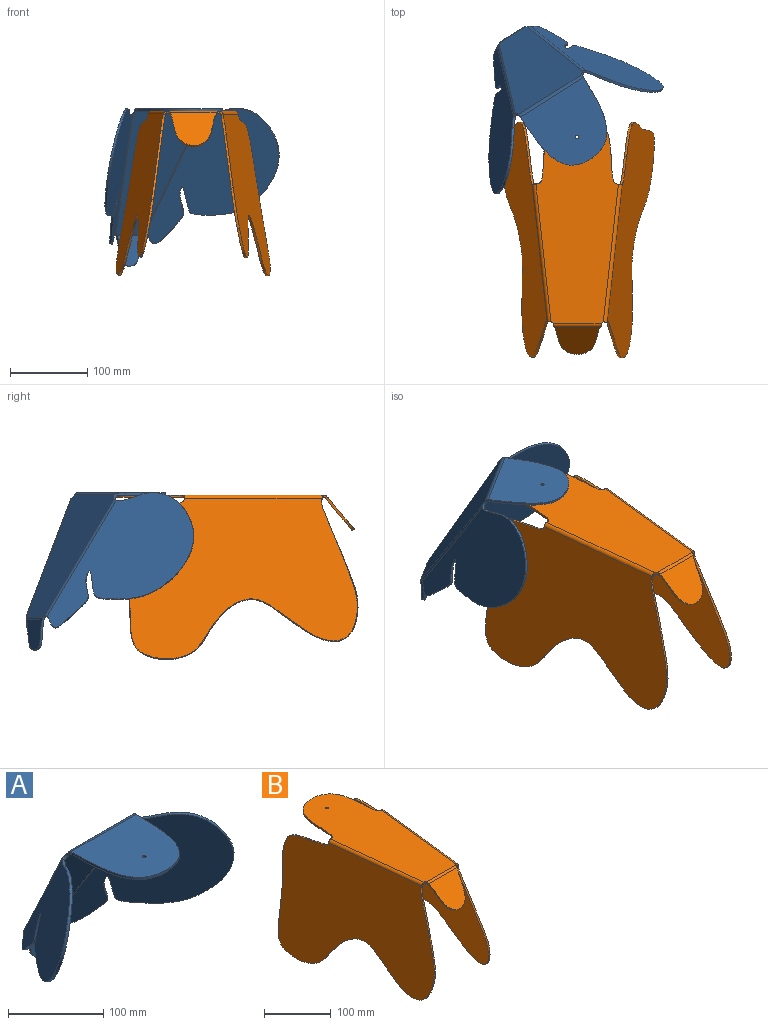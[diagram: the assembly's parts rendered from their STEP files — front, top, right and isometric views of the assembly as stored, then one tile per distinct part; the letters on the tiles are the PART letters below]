
ASSEMBLY  parts=2 mates=1
PART A: 73 faces, bbox 259.7x191.3x206.6 mm
  f0: extruded ~23.99x7.76mm, area 78.3mm2, adj f1,f3,f4,f5
  f1: extruded ~18.34x3.31mm, area 58.3mm2, adj f0,f2,f3,f4
  f2: extruded ~20.11x5.29mm, area 63.3mm2, adj f1,f3,f4,f6
  f3: plane 40.69x38.37mm, normal (0,1,0), area 1160.1mm2, adj f0,f1,f2,f5,f6,f14
  f4: plane 40.69x38.37mm, normal (0,-1,0), area 1160.1mm2, adj f0,f1,f2,f5,f6,f16
  f5: extruded ~14.01x3.09mm, area 43.1mm2, adj f0,f3,f4,f13
  f6: extruded ~16.48x3.39mm, area 50.7mm2, adj f2,f3,f4,f15
  f7: extruded ~6.83x5.68mm, area 21.5mm2, adj f11,f12,f58,f71
  f8: extruded ~4.34x4.24mm, area 12mm2, adj f11,f12,f15,f56
  f9: extruded ~4.06x4.03mm, area 12.1mm2, adj f11,f12,f13,f35
  f10: extruded ~7.14x5.85mm, area 22.4mm2, adj f11,f12,f33,f69
  f11: plane 158.85x103.01mm, normal (0,-0.87,-0.5), area 13392.8mm2, adj f7,f8,f9,f10,f16,f32,f59,f70
  f12: plane 158.85x103.01mm, normal (0,0.87,0.5), area 13392.8mm2, adj f7,f8,f9,f10,f14,f34,f57,f68
  f13: plane 3.27x2.5mm, normal (-1,0,0), area 5.5mm2, adj f5,f9,f14,f16
  f14: cylinder r=5mm len=37.88mm, axis (1,0,0), area 99.2mm2, adj f3,f12,f13,f15
  f15: plane 3.27x2.5mm, normal (1,0,0), area 5.5mm2, adj f6,f8,f14,f16
  f16: cylinder r=2mm len=37.88mm, axis (1,0,0), area 39.7mm2, adj f4,f11,f13,f15
  f17: plane 176.84x161.17mm, normal (-0.75,0.62,0.21), area 17195.4mm2, adj f19,f20,f21,f22,f23,f24,f25,f26
  f18: plane 176.84x161.17mm, normal (0.75,-0.62,-0.21), area 17195.4mm2, adj f19,f20,f21,f22,f23,f24,f25,f26
  f19: extruded ~8.01x6.3mm, area 27.3mm2, adj f17,f18,f35,f36
  f20: extruded ~12.04x8.87mm, area 42.6mm2, adj f17,f18,f21,f36
  f21: plane 20.76x20.45mm, normal (-0.56,-0.44,-0.7), area 87.6mm2, adj f17,f18,f20,f22
  f22: extruded ~24.28x11.41mm, area 83.7mm2, adj f17,f18,f21,f23
  f23: extruded ~24.8x7.62mm, area 77.8mm2, adj f17,f18,f22,f24
  f24: extruded ~18.48x7.77mm, area 56.2mm2, adj f17,f18,f23,f25
  f25: extruded ~17.64x8.77mm, area 56.7mm2, adj f17,f18,f24,f26
  f26: extruded ~14.79x13.54mm, area 52.3mm2, adj f17,f18,f25,f27
  f27: extruded ~87.86x57.74mm, area 373.9mm2, adj f17,f18,f26,f29
  f28: extruded ~14.07x11.88mm, area 48.2mm2, adj f17,f18,f31,f33
  f29: extruded ~49.08x11.13mm, area 153.8mm2, adj f17,f18,f27,f30
  f30: extruded ~28.8x23.75mm, area 119.9mm2, adj f17,f18,f29,f31
  f31: extruded ~44.2x36.25mm, area 168.8mm2, adj f17,f18,f28,f30
  f32: cylinder r=2mm len=150.9mm, axis (0.17,0.49,-0.85), area 307.4mm2, adj f11,f18,f33,f35
  f33: plane 3.77x3.11mm, normal (-0.17,-0.49,0.85), area 9.2mm2, adj f10,f28,f32,f34
  f34: cylinder r=5mm len=151.77mm, axis (0.17,0.49,-0.85), area 768.5mm2, adj f12,f17,f33,f35
  f35: plane 3.77x3.11mm, normal (0.17,0.49,-0.85), area 9.2mm2, adj f9,f19,f32,f34
  f36: extruded ~7.38x7.06mm, area 27.9mm2, adj f17,f18,f19,f20
  f37: extruded ~27.85x21.18mm, area 109.5mm2, adj f38,f51,f53,f54
  f38: extruded ~36.92x10.35mm, area 113.9mm2, adj f37,f39,f53,f54
  f39: extruded ~36.3x22.64mm, area 127.2mm2, adj f38,f40,f53,f54
  f40: extruded ~26.44x22.43mm, area 108mm2, adj f39,f41,f53,f54
  f41: extruded ~44.39x34.78mm, area 164.9mm2, adj f40,f42,f53,f54
  f42: extruded ~17.47x15.89mm, area 63.2mm2, adj f41,f43,f53,f54
  f43: extruded ~8.76x5.78mm, area 27.5mm2, adj f42,f44,f53,f54
  f44: extruded ~19.02x7.48mm, area 57.4mm2, adj f43,f45,f53,f54
  f45: extruded ~8.64x5.55mm, area 27.5mm2, adj f44,f46,f53,f54
  f46: extruded ~24.82x6.78mm, area 76.8mm2, adj f45,f47,f53,f54
  f47: extruded ~12.43x5.06mm, area 36.7mm2, adj f46,f48,f53,f54
  f48: extruded ~12.8x10.64mm, area 46.9mm2, adj f47,f49,f53,f54
  f49: extruded ~20.73x20.47mm, area 87.6mm2, adj f48,f50,f53,f54
  f50: extruded ~12.38x9.32mm, area 43.5mm2, adj f49,f53,f54,f55
  f51: extruded ~45.41x38.2mm, area 176.9mm2, adj f37,f52,f53,f54
  f52: extruded ~15.7x12.92mm, area 54.8mm2, adj f51,f53,f54,f58
  f53: plane 177.09x160.16mm, normal (-0.75,-0.62,-0.21), area 17203.3mm2, adj f37,f38,f39,f40,f41,f42,f43,f44
  f54: plane 177.09x160.16mm, normal (0.75,0.62,0.21), area 17203.3mm2, adj f37,f38,f39,f40,f41,f42,f43,f44
  f55: extruded ~14.65x10.86mm, area 54.4mm2, adj f50,f53,f54,f56
  f56: plane 3.77x3.11mm, normal (-0.17,0.49,-0.85), area 9.2mm2, adj f8,f55,f57,f59
  f57: cylinder r=5mm len=151.78mm, axis (0.17,-0.49,0.85), area 768.8mm2, adj f12,f54,f56,f58
  f58: plane 3.77x3.11mm, normal (0.17,-0.49,0.85), area 9.2mm2, adj f7,f52,f57,f59
  f59: cylinder r=2mm len=150.9mm, axis (0.17,-0.49,0.85), area 307.5mm2, adj f11,f53,f56,f58
  f60: extruded ~10.75x3mm, area 32.3mm2, adj f61,f64,f65,f67
  f61: extruded ~80.79x36.34mm, area 289.2mm2, adj f60,f62,f64,f65
  f62: extruded ~38.1x7.82mm, area 119.2mm2, adj f61,f63,f64,f65
  f63: extruded ~56.09x21.17mm, area 185.4mm2, adj f62,f64,f65,f66
  f64: plane 97.8x95.65mm, normal (0,0,1), area 7819.7mm2, adj f60,f61,f62,f63,f66,f67,f68,f72
  f65: plane 97.8x95.65mm, normal (0,0,-1), area 7819.7mm2, adj f60,f61,f62,f63,f66,f67,f70,f72
  f66: extruded ~30.18x3mm, area 90.7mm2, adj f63,f64,f65,f71
  f67: extruded ~3x1.44mm, area 4.3mm2, adj f60,f64,f65,f69
  f68: cylinder r=5mm len=96.98mm, axis (-1,0,0), area 507.8mm2, adj f12,f64,f69,f71
  f69: plane 4.33x4mm, normal (-1,0,0), area 11mm2, adj f10,f67,f68,f70
  f70: cylinder r=2mm len=96.98mm, axis (-1,0,0), area 203.1mm2, adj f11,f65,f69,f71
  f71: plane 4.33x4mm, normal (1,0,0), area 11mm2, adj f7,f66,f68,f70
  f72: cylinder r=2mm len=4mm, axis (0,0,1), area 37.7mm2, adj f64,f65
PART B: 70 faces, bbox 199.4x320.8x215.7 mm
  f0: extruded ~12.02x10.77mm, area 40.1mm2, adj f1,f4,f5,f7
  f1: extruded ~27.06x23.39mm, area 112.6mm2, adj f0,f2,f4,f5
  f2: extruded ~30.34x13.13mm, area 110.4mm2, adj f1,f3,f4,f5
  f3: extruded ~19.76x17.26mm, area 72.1mm2, adj f2,f4,f5,f6
  f4: plane 62.03x44.64mm, normal (0,0.77,-0.64), area 2504.5mm2, adj f0,f1,f2,f3,f6,f7,f11
  f5: plane 62.03x44.64mm, normal (0,-0.77,0.64), area 2504.5mm2, adj f0,f1,f2,f3,f6,f7,f9
  f6: extruded ~15.56x13.74mm, area 55.7mm2, adj f3,f4,f5,f8
  f7: extruded ~7.36x6.86mm, area 23.3mm2, adj f0,f4,f5,f10
  f8: plane 3.83x3.71mm, normal (-1,0,0), area 9.2mm2, adj f6,f9,f11,f20
  f9: cylinder r=5mm len=61.53mm, axis (1,0,0), area 268.5mm2, adj f5,f8,f10,f22
  f10: plane 3.83x3.71mm, normal (1,0,0), area 9.2mm2, adj f7,f9,f11,f19
  f11: cylinder r=2mm len=61.53mm, axis (1,0,0), area 107.4mm2, adj f4,f8,f10,f21
  f12: extruded ~52.99x11.82mm, area 164.6mm2, adj f13,f14,f16,f17
  f13: extruded ~38.1x30.2mm, area 162.5mm2, adj f12,f16,f17,f18
  f14: extruded ~69.53x28.96mm, area 225.8mm2, adj f12,f15,f16,f17
  f15: extruded ~26.25x7.13mm, area 82.3mm2, adj f14,f16,f17,f34
  f16: plane 306.13x211.08mm, normal (-0.98,0.11,-0.17), area 48358mm2, adj f12,f13,f14,f15,f18,f35,f37,f38
  f17: plane 306.13x211.08mm, normal (0.98,-0.11,0.17), area 48358mm2, adj f12,f13,f14,f15,f18,f33,f37,f38
  f18: extruded ~30.85x10.09mm, area 97.3mm2, adj f13,f16,f17,f37
  f19: extruded ~3x2.89mm, area 11.2mm2, adj f10,f21,f22,f34
  f20: extruded ~3.31x3mm, area 13mm2, adj f8,f21,f22,f53
  f21: plane 275.63x106.54mm, normal (0,0,-1), area 23059.1mm2, adj f11,f19,f20,f27,f28,f29,f30,f31
  f22: plane 275.63x106.54mm, normal (0,0,1), area 23059.1mm2, adj f9,f19,f20,f27,f28,f29,f30,f31
  f23: plane 305.98x209.65mm, normal (-0.98,-0.11,0.17), area 48219.4mm2, adj f25,f26,f50,f54,f55,f56,f57,f58
  f24: plane 305.98x209.65mm, normal (0.98,0.11,-0.17), area 48219.4mm2, adj f25,f26,f52,f54,f55,f56,f57,f58
  f25: extruded ~20.81x6.12mm, area 64.2mm2, adj f23,f24,f53,f68
  f26: extruded ~41.3x12.41mm, area 130.8mm2, adj f23,f24,f65,f69
  f27: extruded ~14.82x8.11mm, area 56.4mm2, adj f21,f22,f28,f36
  f28: extruded ~59.97x9.53mm, area 183.8mm2, adj f21,f22,f27,f29
  f29: extruded ~27.16x19.05mm, area 103.1mm2, adj f21,f22,f28,f30
  f30: extruded ~35.63x10.34mm, area 115mm2, adj f21,f22,f29,f31
  f31: extruded ~65.62x16.93mm, area 209.5mm2, adj f21,f22,f30,f32
  f32: extruded ~18.35x9.17mm, area 69.1mm2, adj f21,f22,f31,f51
  f33: cylinder r=5mm len=178.33mm, axis (-0.11,-0.99,0), area 1248.6mm2, adj f17,f22,f34,f36
  f34: plane 4.9x4.65mm, normal (-0.11,-0.99,0), area 14.7mm2, adj f15,f19,f33,f35
  f35: cylinder r=2mm len=178.01mm, axis (-0.11,-0.99,0), area 499.5mm2, adj f16,f21,f34,f36
  f36: plane 4.9x4.65mm, normal (0.11,0.99,0), area 14.7mm2, adj f27,f33,f35,f49
  f37: extruded ~45.76x32.28mm, area 166.5mm2, adj f16,f17,f18,f38
  f38: extruded ~26.69x13.13mm, area 88.6mm2, adj f16,f17,f37,f39
  f39: extruded ~43.78x20.87mm, area 151.5mm2, adj f16,f17,f38,f40
  f40: extruded ~19.2x14.72mm, area 72.3mm2, adj f16,f17,f39,f41
  f41: extruded ~21.07x13.48mm, area 74.9mm2, adj f16,f17,f40,f42
  f42: extruded ~76.97x18.68mm, area 252.7mm2, adj f16,f17,f41,f43
  f43: extruded ~45.58x13.86mm, area 148.3mm2, adj f16,f17,f42,f44
  f44: extruded ~44.3x10.52mm, area 133.4mm2, adj f16,f17,f43,f45
  f45: extruded ~40.57x9.4mm, area 123mm2, adj f16,f17,f44,f46
  f46: extruded ~43.45x10.52mm, area 132.2mm2, adj f16,f17,f45,f47
  f47: extruded ~41.71x17.33mm, area 143.6mm2, adj f16,f17,f46,f48
  f48: extruded ~21.31x5.57mm, area 63.7mm2, adj f16,f17,f47,f49
  f49: extruded ~15.9x8.95mm, area 58.3mm2, adj f16,f17,f36,f48
  f50: cylinder r=5mm len=178.33mm, axis (-0.11,0.99,0), area 1248.6mm2, adj f22,f23,f51,f53
  f51: plane 4.9x4.65mm, normal (-0.11,0.99,0), area 14.7mm2, adj f32,f50,f52,f54
  f52: cylinder r=2mm len=178.01mm, axis (-0.11,0.99,0), area 499.5mm2, adj f21,f24,f51,f53
  f53: plane 4.9x4.65mm, normal (0.11,-0.99,0), area 14.7mm2, adj f20,f25,f50,f52
  f54: extruded ~15.49x8.3mm, area 55.7mm2, adj f23,f24,f51,f55
  f55: extruded ~20.61x5.51mm, area 61.7mm2, adj f23,f24,f54,f56
  f56: extruded ~37.05x8.76mm, area 115.5mm2, adj f23,f24,f55,f57
  f57: extruded ~45.5x11.63mm, area 143.6mm2, adj f23,f24,f56,f58
  f58: extruded ~40.26x9.3mm, area 122.2mm2, adj f23,f24,f57,f59
  f59: extruded ~43.64x10.36mm, area 131.4mm2, adj f23,f24,f58,f60
  f60: extruded ~83.92x62.27mm, area 394.1mm2, adj f23,f24,f59,f61
  f61: extruded ~17.24x13.48mm, area 65.5mm2, adj f23,f24,f60,f62
  f62: extruded ~34.37x25.98mm, area 130.5mm2, adj f23,f24,f61,f63
  f63: extruded ~41.56x16.31mm, area 138.7mm2, adj f23,f24,f62,f64
  f64: extruded ~34.51x20.25mm, area 119.4mm2, adj f23,f24,f63,f65
  f65: extruded ~31.84x22.41mm, area 115.2mm2, adj f23,f24,f26,f64
  f66: cylinder r=2mm len=4mm, axis (0,0,1), area 37.7mm2, adj f21,f22
  f67: extruded ~43.56x10.07mm, area 133.1mm2, adj f23,f24,f68,f69
  f68: extruded ~90.19x36.26mm, area 292.2mm2, adj f23,f24,f25,f67
  f69: extruded ~30.91x22.49mm, area 122.3mm2, adj f23,f24,f26,f67
PLACE A rot(axis=(0,0,1),32.2deg) t=(63.07,-73.23,28.73)mm
PLACE B t=(39.66,63.55,25.73)mm fixed
MATE revolute B.f66 <-> A.f72  axis (0,0,1) through (25.9,-38.25,28.73)mm
